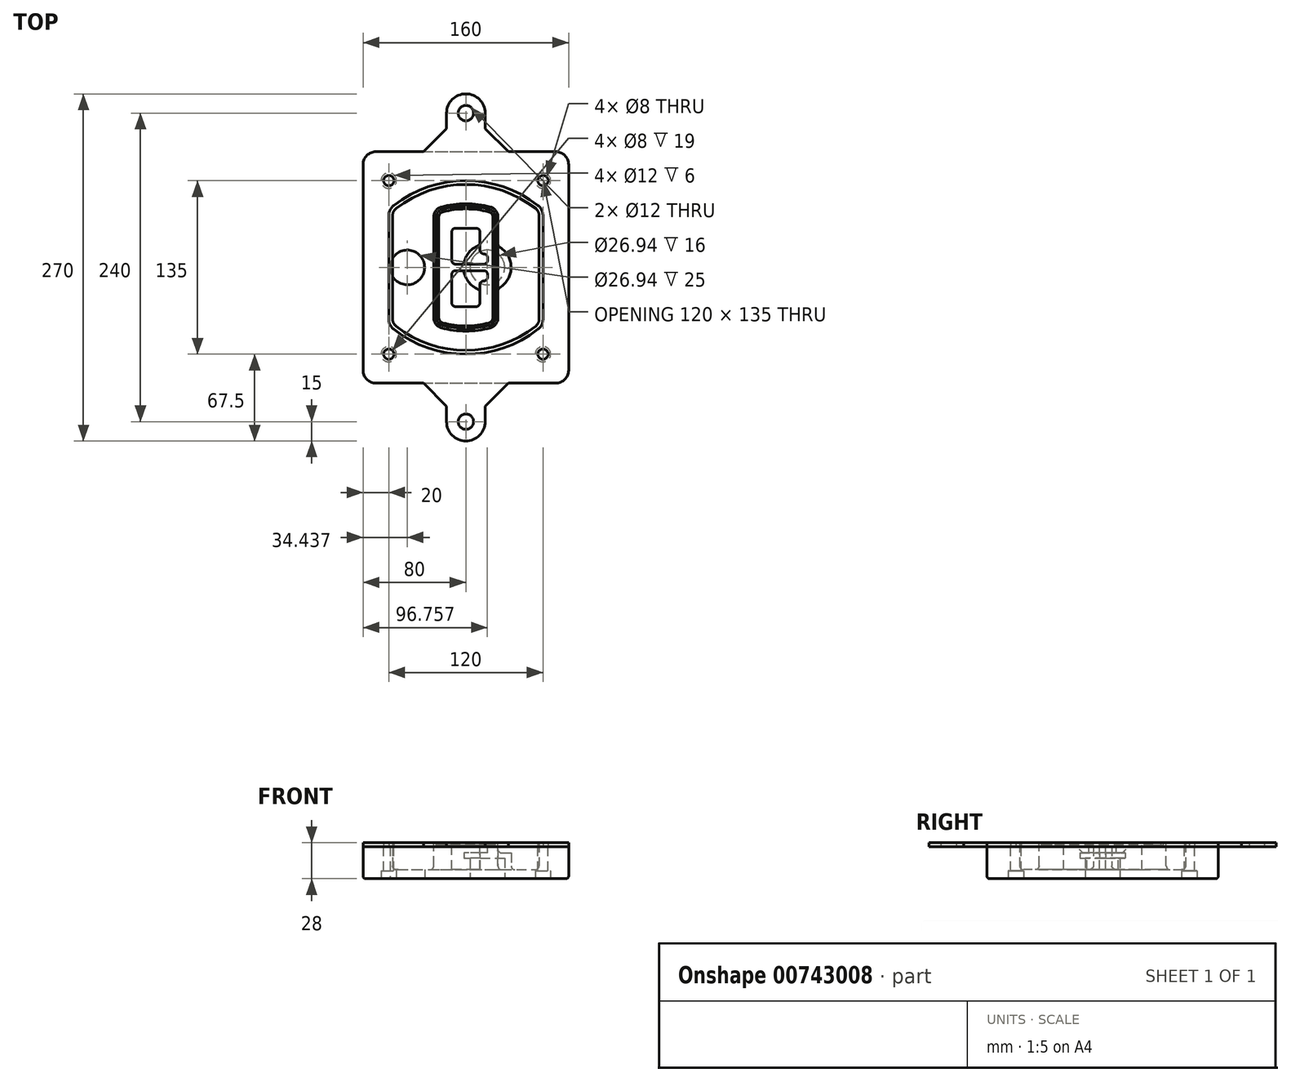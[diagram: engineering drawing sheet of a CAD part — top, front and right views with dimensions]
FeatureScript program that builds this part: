
annotation { "Feature Type Name" : "Feature", "Feature Type Description" : "" }
export const myFeature = defineFeature(function(context is Context, id is Id, definition is map)
    precondition{}
    {
        {
            var Q0;
            Q0=qCreatedBy(makeId("Top.planeOp"),FACE);
            var sketch = newSketch(context, id + "F0", { "sketchPlane" : qUnion([Q0])});
            skPoint(sketch, "E0.rect.middle", {"position": v(0, 0) * mm});
            skLineSegment(sketch, "E1.bottom", {"start": v(-70, -90) * mm, "end": v(70, -90) * mm});
            skLineSegment(sketch, "E1.top", {"start": v(-70, 90) * mm, "end": v(70, 90) * mm});
            skLineSegment(sketch, "E1.left", {"start": v(-80, -80) * mm, "end": v(-80, 80) * mm});
            skLineSegment(sketch, "E1.right", {"start": v(80, -80) * mm, "end": v(80, 80) * mm});
            skLineSegment(sketch, "E2", {"start": v(-80, 90) * mm, "end": v(80, -90) * mm, "construction": true});
            skLineSegment(sketch, "E3", {"start": v(80, 90) * mm, "end": v(-80, -90) * mm, "construction": true});
            skCircle(sketch, "E4", {"center": v(-60, 67.5) * mm, "radius": 4 * mm});
            skCircle(sketch, "E5", {"center": v(60, 67.5) * mm, "radius": 4 * mm});
            skCircle(sketch, "E6", {"center": v(60, -67.5) * mm, "radius": 4 * mm});
            skCircle(sketch, "E7", {"center": v(-60, -67.5) * mm, "radius": 4 * mm});
            skLineSegment(sketch, "E8", {"start": v(-60, 67.5) * mm, "end": v(60, 67.5) * mm, "construction": true});
            skLineSegment(sketch, "E9", {"start": v(60, 67.5) * mm, "end": v(60, -67.5) * mm, "construction": true});
            skLineSegment(sketch, "E10", {"start": v(60, -67.5) * mm, "end": v(-60, -67.5) * mm, "construction": true});
            skLineSegment(sketch, "E11", {"start": v(-60, -67.5) * mm, "end": v(-60, 67.5) * mm, "construction": true});
            skLineSegment(sketch, "E12", {"start": v(-60, 40.3) * mm, "end": v(-60, -40.3) * mm});
            skLineSegment(sketch, "E13", {"start": v(60, 40.3) * mm, "end": v(60, -40.3) * mm});
            skArc(sketch, "E14", {"start": v(56.15, 48.18) * mm, "mid": v(0, 67.5) * mm, "end": v(-56.15, 48.18) * mm});
            skArc(sketch, "E15", {"start": v(-56.15, -48.18) * mm, "mid": v(0, -67.5) * mm, "end": v(56.15, -48.18) * mm});
            skLineSegment(sketch, "E16", {"start": v(-60, 0) * mm, "end": v(60, 0) * mm, "construction": true});
            skPoint(sketch, "E17.visualSharp", {"position": v(-60, -45) * mm});
            skArc(sketch, "E17.filletArc", {"start": v(-60, -40.3) * mm, "mid": v(-58.99, -44.68) * mm, "end": v(-56.15, -48.18) * mm});
            skPoint(sketch, "E18.visualSharp", {"position": v(-60, 45) * mm});
            skArc(sketch, "E18.filletArc", {"start": v(-56.15, 48.18) * mm, "mid": v(-58.99, 44.68) * mm, "end": v(-60, 40.3) * mm});
            skPoint(sketch, "E19.visualSharp", {"position": v(60, 45) * mm});
            skArc(sketch, "E19.filletArc", {"start": v(60, 40.3) * mm, "mid": v(58.99, 44.68) * mm, "end": v(56.15, 48.18) * mm});
            skPoint(sketch, "E20.visualSharp", {"position": v(60, -45) * mm});
            skArc(sketch, "E20.filletArc", {"start": v(56.15, -48.18) * mm, "mid": v(58.99, -44.68) * mm, "end": v(60, -40.3) * mm});
            skPoint(sketch, "E21.visualSharp", {"position": v(-80, 90) * mm});
            skArc(sketch, "E21.filletArc", {"start": v(-70, 90) * mm, "mid": v(-77.07, 87.07) * mm, "end": v(-80, 80) * mm});
            skPoint(sketch, "E22.visualSharp", {"position": v(80, 90) * mm});
            skArc(sketch, "E22.filletArc", {"start": v(80, 80) * mm, "mid": v(77.07, 87.07) * mm, "end": v(70, 90) * mm});
            skPoint(sketch, "E23.visualSharp", {"position": v(80, -90) * mm});
            skArc(sketch, "E23.filletArc", {"start": v(70, -90) * mm, "mid": v(77.07, -87.07) * mm, "end": v(80, -80) * mm});
            skPoint(sketch, "E24.visualSharp", {"position": v(-80, -90) * mm});
            skArc(sketch, "E24.filletArc", {"start": v(-80, -80) * mm, "mid": v(-77.07, -87.07) * mm, "end": v(-70, -90) * mm});
            skArc(sketch, "E25.0", {"start": v(57, 40.3) * mm, "mid": v(56.3, 43.36) * mm, "end": v(54.3, 45.81) * mm});
            skLineSegment(sketch, "E25.1", {"start": v(57, 40.3) * mm, "end": v(57, -40.3) * mm});
            skArc(sketch, "E25.2", {"start": v(54.3, -45.81) * mm, "mid": v(56.3, -43.36) * mm, "end": v(57, -40.3) * mm});
            skArc(sketch, "E25.3", {"start": v(-54.3, -45.81) * mm, "mid": v(0, -64.5) * mm, "end": v(54.3, -45.81) * mm});
            skArc(sketch, "E25.4", {"start": v(-57, -40.3) * mm, "mid": v(-56.3, -43.36) * mm, "end": v(-54.3, -45.81) * mm});
            skArc(sketch, "E25.5", {"start": v(54.3, 45.81) * mm, "mid": v(0, 64.5) * mm, "end": v(-54.3, 45.81) * mm});
            skLineSegment(sketch, "E25.6", {"start": v(-57, 40.3) * mm, "end": v(-57, -40.3) * mm});
            skArc(sketch, "E25.7", {"start": v(-54.3, 45.81) * mm, "mid": v(-56.3, 43.36) * mm, "end": v(-57, 40.3) * mm});
            skArc(sketch, "E26.0", {"start": v(-58.62, 51.33) * mm, "mid": v(-62.58, 46.43) * mm, "end": v(-64, 40.3) * mm});
            skArc(sketch, "E26.1", {"start": v(58.62, 51.33) * mm, "mid": v(0, 71.5) * mm, "end": v(-58.62, 51.33) * mm});
            skArc(sketch, "E26.2", {"start": v(64, 40.3) * mm, "mid": v(62.58, 46.43) * mm, "end": v(58.62, 51.33) * mm});
            skLineSegment(sketch, "E26.3", {"start": v(64, 40.3) * mm, "end": v(64, -40.3) * mm});
            skArc(sketch, "E26.4", {"start": v(58.62, -51.33) * mm, "mid": v(62.58, -46.43) * mm, "end": v(64, -40.3) * mm});
            skLineSegment(sketch, "E26.5", {"start": v(-64, 40.3) * mm, "end": v(-64, -40.3) * mm});
            skArc(sketch, "E26.6", {"start": v(-58.62, -51.33) * mm, "mid": v(0, -71.5) * mm, "end": v(58.62, -51.33) * mm});
            skArc(sketch, "E26.7", {"start": v(-64, -40.3) * mm, "mid": v(-62.58, -46.43) * mm, "end": v(-58.62, -51.33) * mm});
            skSolve(sketch);
        }
        {
            var Q0;
            Q0=makeQuery(id+"F0.imprint","IMPRINT",FACE,{"disambiguationData":[TD([[makeQuery(id+"F0.imprint","IMPRINT",EDGE,{"derivedFrom":sQuery(id+"F0.wireOp",EDGE,"E1.bottom")}),1.0]])]});
            var Q1;
            Q1=makeQuery(id+"F0.imprint","IMPRINT",FACE,{"disambiguationData":[TD([[makeQuery(id+"F0.imprint","IMPRINT",EDGE,{"derivedFrom":sQuery(id+"F0.wireOp",EDGE,"E12")}),1.0]])]});
            var Q2;
            Q2=makeQuery(id+"F0.imprint","IMPRINT",FACE,{"disambiguationData":[TD([[makeQuery(id+"F0.imprint","IMPRINT",EDGE,{"derivedFrom":sQuery(id+"F0.wireOp",EDGE,"E25.0")}),1.0]])]});
            var Q3;
            Q3=makeQuery(id+"F0.imprint","IMPRINT",FACE,{"disambiguationData":[TD([[makeQuery(id+"F0.imprint","IMPRINT",EDGE,{"derivedFrom":sQuery(id+"F0.wireOp",EDGE,"E12")}),-1.0]])]});
            extrude(context, id + "F1", {"entities" : qUnion([Q0, Q1, Q2, Q3]), "oppositeDirection" : true, "depth" : 25 * mm, "offsetDistance" : 25 * mm});
        }
        {
            var Q0;
            Q0=makeQuery(id+"F0.imprint","IMPRINT",FACE,{"disambiguationData":[TD([[makeQuery(id+"F0.imprint","IMPRINT",EDGE,{"derivedFrom":sQuery(id+"F0.wireOp",EDGE,"E12")}),1.0]])]});
            extrude(context, id + "F2", {"entities" : qUnion([Q0]), "operationType" : NewBodyOperationType.ADD, "depth" : 3 * mm, "offsetDistance" : 25 * mm});
        }
        {
            var Q0;
            Q0=makeQuery(id+"F0.imprint","IMPRINT",FACE,{"disambiguationData":[TD([[makeQuery(id+"F0.imprint","IMPRINT",EDGE,{"derivedFrom":sQuery(id+"F0.wireOp",EDGE,"E25.0")}),1.0]])]});
            extrude(context, id + "F3", {"entities" : qUnion([Q0]), "operationType" : NewBodyOperationType.REMOVE, "oppositeDirection" : true, "depth" : 18 * mm});
        }
        {
            var Q0;
            Q0=makeQuery(id+"F2.opExtrude","CAP_FACE",FACE,{"disambiguationData":[OSD([sQuery(id+"F0.wireOp",EDGE,"E12"),sQuery(id+"F0.wireOp",EDGE,"E13"),sQuery(id+"F0.wireOp",EDGE,"E14"),sQuery(id+"F0.wireOp",EDGE,"E15"),sQuery(id+"F0.wireOp",EDGE,"E17.filletArc"),sQuery(id+"F0.wireOp",EDGE,"E18.filletArc"),sQuery(id+"F0.wireOp",EDGE,"E19.filletArc"),sQuery(id+"F0.wireOp",EDGE,"E20.filletArc"),sQuery(id+"F0.wireOp",EDGE,"E25.0"),sQuery(id+"F0.wireOp",EDGE,"E25.1"),sQuery(id+"F0.wireOp",EDGE,"E25.2"),sQuery(id+"F0.wireOp",EDGE,"E25.3"),sQuery(id+"F0.wireOp",EDGE,"E25.4"),sQuery(id+"F0.wireOp",EDGE,"E25.5"),sQuery(id+"F0.wireOp",EDGE,"E25.6"),sQuery(id+"F0.wireOp",EDGE,"E25.7")])],"isStart":false});
            var sketch = newSketch(context, id + "F4", { "sketchPlane" : qUnion([Q0])});
            skArc(sketch, "E27.0", {"start": v(-19.08, -46.97) * mm, "mid": v(0, -49.5) * mm, "end": v(19.08, -46.97) * mm});
            skArc(sketch, "E28.0", {"start": v(19.08, 46.97) * mm, "mid": v(0, 49.5) * mm, "end": v(-19.08, 46.97) * mm});
            skLineSegment(sketch, "E29", {"start": v(-25, 39.25) * mm, "end": v(-25, -39.25) * mm});
            skLineSegment(sketch, "E30", {"start": v(25, 39.25) * mm, "end": v(25, -39.25) * mm});
            skLineSegment(sketch, "E31", {"start": v(-25, 45.1) * mm, "end": v(25, 45.1) * mm, "construction": true});
            skLineSegment(sketch, "E32", {"start": v(-25, -45.1) * mm, "end": v(25, -45.1) * mm, "construction": true});
            skPoint(sketch, "E33.visualSharp", {"position": v(-25, 45.1) * mm});
            skArc(sketch, "E33.filletArc", {"start": v(-19.08, 46.97) * mm, "mid": v(-23.35, 44.11) * mm, "end": v(-25, 39.25) * mm});
            skPoint(sketch, "E34.visualSharp", {"position": v(25, 45.1) * mm});
            skArc(sketch, "E34.filletArc", {"start": v(25, 39.25) * mm, "mid": v(23.35, 44.11) * mm, "end": v(19.08, 46.97) * mm});
            skPoint(sketch, "E35.visualSharp", {"position": v(25, -45.1) * mm});
            skArc(sketch, "E35.filletArc", {"start": v(19.08, -46.97) * mm, "mid": v(23.35, -44.11) * mm, "end": v(25, -39.25) * mm});
            skPoint(sketch, "E36.visualSharp", {"position": v(-25, -45.1) * mm});
            skArc(sketch, "E36.filletArc", {"start": v(-25, -39.25) * mm, "mid": v(-23.35, -44.11) * mm, "end": v(-19.08, -46.97) * mm});
            skArc(sketch, "E37.0", {"start": v(54.3, 45.81) * mm, "mid": v(0, 64.5) * mm, "end": v(-54.3, 45.81) * mm});
            skArc(sketch, "E37.1", {"start": v(-54.3, 45.81) * mm, "mid": v(-56.3, 43.36) * mm, "end": v(-57, 40.3) * mm});
            skLineSegment(sketch, "E37.2", {"start": v(-57, 40.3) * mm, "end": v(-57, -40.3) * mm});
            skArc(sketch, "E37.3", {"start": v(-57, -40.3) * mm, "mid": v(-56.3, -43.36) * mm, "end": v(-54.3, -45.81) * mm});
            skArc(sketch, "E37.4", {"start": v(-54.3, -45.81) * mm, "mid": v(0, -64.5) * mm, "end": v(54.3, -45.81) * mm});
            skArc(sketch, "E37.5", {"start": v(54.3, -45.81) * mm, "mid": v(56.3, -43.36) * mm, "end": v(57, -40.3) * mm});
            skLineSegment(sketch, "E37.6", {"start": v(57, 40.3) * mm, "end": v(57, -40.3) * mm});
            skArc(sketch, "E37.7", {"start": v(57, 40.3) * mm, "mid": v(56.3, 43.36) * mm, "end": v(54.3, 45.81) * mm});
            skLineSegment(sketch, "E38.0", {"start": v(23, 39.25) * mm, "end": v(23, -39.25) * mm});
            skArc(sketch, "E38.1", {"start": v(18.56, -45.04) * mm, "mid": v(21.76, -42.9) * mm, "end": v(23, -39.25) * mm});
            skArc(sketch, "E38.2", {"start": v(-18.56, -45.04) * mm, "mid": v(0, -47.5) * mm, "end": v(18.56, -45.04) * mm});
            skArc(sketch, "E38.3", {"start": v(-23, -39.25) * mm, "mid": v(-21.76, -42.9) * mm, "end": v(-18.56, -45.04) * mm});
            skLineSegment(sketch, "E38.4", {"start": v(-23, 39.25) * mm, "end": v(-23, -39.25) * mm});
            skArc(sketch, "E38.5", {"start": v(23, 39.25) * mm, "mid": v(21.76, 42.9) * mm, "end": v(18.56, 45.04) * mm});
            skArc(sketch, "E38.6", {"start": v(-18.56, 45.04) * mm, "mid": v(-21.76, 42.9) * mm, "end": v(-23, 39.25) * mm});
            skArc(sketch, "E38.7", {"start": v(18.56, 45.04) * mm, "mid": v(0, 47.5) * mm, "end": v(-18.56, 45.04) * mm});
            skArc(sketch, "E39.0", {"start": v(21, 39.25) * mm, "mid": v(20.18, 41.68) * mm, "end": v(18.04, 43.1) * mm});
            skLineSegment(sketch, "E39.1", {"start": v(21, 39.25) * mm, "end": v(21, -39.25) * mm});
            skArc(sketch, "E39.2", {"start": v(18.04, -43.1) * mm, "mid": v(20.18, -41.68) * mm, "end": v(21, -39.25) * mm});
            skArc(sketch, "E39.3", {"start": v(-18.04, -43.1) * mm, "mid": v(0, -45.5) * mm, "end": v(18.04, -43.1) * mm});
            skArc(sketch, "E39.4", {"start": v(-21, -39.25) * mm, "mid": v(-20.18, -41.68) * mm, "end": v(-18.04, -43.1) * mm});
            skArc(sketch, "E39.5", {"start": v(18.04, 43.1) * mm, "mid": v(0, 45.5) * mm, "end": v(-18.04, 43.1) * mm});
            skLineSegment(sketch, "E39.6", {"start": v(-21, 39.25) * mm, "end": v(-21, -39.25) * mm});
            skArc(sketch, "E39.7", {"start": v(-18.04, 43.1) * mm, "mid": v(-20.18, 41.68) * mm, "end": v(-21, 39.25) * mm});
            skLineSegment(sketch, "E40", {"start": v(-25, 0) * mm, "end": v(25, 0) * mm, "construction": true});
            skLineSegment(sketch, "E41", {"start": v(-11, 5.5) * mm, "end": v(-11, 27.5) * mm});
            skLineSegment(sketch, "E42", {"start": v(-8, 30.5) * mm, "end": v(8, 30.5) * mm});
            skLineSegment(sketch, "E43", {"start": v(11, 27.5) * mm, "end": v(11, 13.5) * mm});
            skLineSegment(sketch, "E44", {"start": v(14, 10.5) * mm, "end": v(14, 10.5) * mm});
            skLineSegment(sketch, "E45", {"start": v(17, 7.5) * mm, "end": v(17, 5.5) * mm});
            skLineSegment(sketch, "E46", {"start": v(14, 2.5) * mm, "end": v(-8, 2.5) * mm});
            skPoint(sketch, "E47.visualSharp", {"position": v(-11, 30.5) * mm});
            skArc(sketch, "E47.filletArc", {"start": v(-8, 30.5) * mm, "mid": v(-10.12, 29.62) * mm, "end": v(-11, 27.5) * mm});
            skPoint(sketch, "E48.visualSharp", {"position": v(11, 30.5) * mm});
            skArc(sketch, "E48.filletArc", {"start": v(11, 27.5) * mm, "mid": v(10.12, 29.62) * mm, "end": v(8, 30.5) * mm});
            skPoint(sketch, "E49.visualSharp", {"position": v(11, 10.5) * mm});
            skArc(sketch, "E49.filletArc", {"start": v(11, 13.5) * mm, "mid": v(11.88, 11.38) * mm, "end": v(14, 10.5) * mm});
            skPoint(sketch, "E50.visualSharp", {"position": v(17, 10.5) * mm});
            skArc(sketch, "E50.filletArc", {"start": v(17, 7.5) * mm, "mid": v(16.12, 9.62) * mm, "end": v(14, 10.5) * mm});
            skPoint(sketch, "E51.visualSharp", {"position": v(17, 2.5) * mm});
            skArc(sketch, "E51.filletArc", {"start": v(14, 2.5) * mm, "mid": v(16.12, 3.38) * mm, "end": v(17, 5.5) * mm});
            skPoint(sketch, "E52.visualSharp", {"position": v(-11, 2.5) * mm});
            skArc(sketch, "E52.filletArc", {"start": v(-11, 5.5) * mm, "mid": v(-10.12, 3.38) * mm, "end": v(-8, 2.5) * mm});
            skLineSegment(sketch, "E53.0.MirrorCS", {"start": v(14, -2.5) * mm, "end": v(-8, -2.5) * mm});
            skArc(sketch, "E54.0.MirrorCS", {"start": v(-11, -5.5) * mm, "mid": v(-10.12, -3.38) * mm, "end": v(-8, -2.5) * mm});
            skLineSegment(sketch, "E55.0.MirrorCS", {"start": v(-11, -5.5) * mm, "end": v(-11, -27.5) * mm});
            skArc(sketch, "E56.0.MirrorCS", {"start": v(-8, -30.5) * mm, "mid": v(-10.12, -29.62) * mm, "end": v(-11, -27.5) * mm});
            skLineSegment(sketch, "E57.0.MirrorCS", {"start": v(-8, -30.5) * mm, "end": v(8, -30.5) * mm});
            skArc(sketch, "E58.0.MirrorCS", {"start": v(11, -27.5) * mm, "mid": v(10.12, -29.62) * mm, "end": v(8, -30.5) * mm});
            skLineSegment(sketch, "E59.0.MirrorCS", {"start": v(11, -27.5) * mm, "end": v(11, -13.5) * mm});
            skArc(sketch, "E60.0.MirrorCS", {"start": v(11, -13.5) * mm, "mid": v(11.88, -11.38) * mm, "end": v(14, -10.5) * mm});
            skArc(sketch, "E61.0.MirrorCS", {"start": v(17, -7.5) * mm, "mid": v(16.12, -9.62) * mm, "end": v(14, -10.5) * mm});
            skLineSegment(sketch, "E62.0.MirrorCS", {"start": v(17, -7.5) * mm, "end": v(17, -5.5) * mm});
            skArc(sketch, "E63.0.MirrorCS", {"start": v(14, -2.5) * mm, "mid": v(16.12, -3.38) * mm, "end": v(17, -5.5) * mm});
            skSolve(sketch);
        }
        {
            var Q0;
            Q0=makeQuery(id+"F4.imprint","IMPRINT",FACE,{"disambiguationData":[TD([[makeQuery(id+"F4.imprint","IMPRINT",EDGE,{"derivedFrom":sQuery(id+"F4.wireOp",EDGE,"E27.0")}),1.0]])]});
            var Q1;
            Q1=makeQuery(id+"F4.imprint","IMPRINT",FACE,{"disambiguationData":[TD([[makeQuery(id+"F4.imprint","IMPRINT",EDGE,{"derivedFrom":sQuery(id+"F4.wireOp",EDGE,"E38.0")}),-1.0]])]});
            var Q2;
            Q2=makeQuery(id+"F4.imprint","IMPRINT",FACE,{"disambiguationData":[TD([[makeQuery(id+"F4.imprint","IMPRINT",EDGE,{"derivedFrom":sQuery(id+"F4.wireOp",EDGE,"E39.0")}),1.0]])]});
            extrude(context, id + "F5", {"entities" : qUnion([Q0, Q1, Q2]), "operationType" : NewBodyOperationType.ADD, "endBound" : BoundingType.UP_TO_NEXT, "oppositeDirection" : true, "depth" : 25 * mm});
        }
        {
            var Q0;
            Q0=makeQuery(id+"F4.imprint","IMPRINT",FACE,{"disambiguationData":[TD([[makeQuery(id+"F4.imprint","IMPRINT",EDGE,{"derivedFrom":sQuery(id+"F4.wireOp",EDGE,"E38.0")}),-1.0]])]});
            extrude(context, id + "F6", {"entities" : qUnion([Q0]), "operationType" : NewBodyOperationType.REMOVE, "oppositeDirection" : true, "depth" : 2 * mm});
        }
        {
            var Q0;
            Q0=makeQuery(id+"F1.opExtrude","CAP_FACE",FACE,{"disambiguationData":[OSD([sQuery(id+"F0.wireOp",EDGE,"E1.bottom"),sQuery(id+"F0.wireOp",EDGE,"E1.top"),sQuery(id+"F0.wireOp",EDGE,"E1.left"),sQuery(id+"F0.wireOp",EDGE,"E1.right"),sQuery(id+"F0.wireOp",EDGE,"E4"),sQuery(id+"F0.wireOp",EDGE,"E5"),sQuery(id+"F0.wireOp",EDGE,"E6"),sQuery(id+"F0.wireOp",EDGE,"E7"),sQuery(id+"F0.wireOp",EDGE,"E21.filletArc"),sQuery(id+"F0.wireOp",EDGE,"E22.filletArc"),sQuery(id+"F0.wireOp",EDGE,"E23.filletArc"),sQuery(id+"F0.wireOp",EDGE,"E24.filletArc")])],"isStart":false});
            var sketch = newSketch(context, id + "F7", { "sketchPlane" : qUnion([Q0])});
            skCircle(sketch, "E64", {"center": v(16.76, 0) * mm, "radius": 13.47 * mm});
            skCircle(sketch, "E65", {"center": v(-45.56, 0) * mm, "radius": 13.47 * mm});
            skLineSegment(sketch, "E66", {"start": v(80, 0) * mm, "end": v(-80, 0) * mm});
            skCircle(sketch, "E67", {"center": v(16.76, 0) * mm, "radius": 18.47 * mm});
            skCircle(sketch, "E68", {"center": v(60, -67.5) * mm, "radius": 6 * mm});
            skCircle(sketch, "E69", {"center": v(-60, -67.5) * mm, "radius": 6 * mm});
            skCircle(sketch, "E70", {"center": v(-60, 67.5) * mm, "radius": 6 * mm});
            skCircle(sketch, "E71", {"center": v(60, 67.5) * mm, "radius": 6 * mm});
            skSolve(sketch);
        }
        {
            var Q0;
            {var subQ1=sQuery(id+"F7.wireOp",EDGE,"E66");var subQ4=sQuery(id+"F7.wireOp",EDGE,"E64");var subQ6=makeQuery(id+"F7.imprint","INTERSECT",VERTEX,{"disambiguationData":[OD(0.0)],"derivedFrom":[subQ4,subQ1]});Q0=makeQuery(id+"F7.imprint","IMPRINT",FACE,{"disambiguationData":[TD([[makeQuery(id+"F7.imprint","IMPRINT",EDGE,{"disambiguationData":[TD([[subQ6,-1.0]])],"derivedFrom":subQ4}),-1.0]])]});}
            var Q1;
            {var subQ0=sQuery(id+"F7.wireOp",EDGE,"E66");var subQ1=sQuery(id+"F7.wireOp",EDGE,"E64");var subQ3=makeQuery(id+"F7.imprint","INTERSECT",VERTEX,{"disambiguationData":[OD(0.0)],"derivedFrom":[subQ1,subQ0]});Q1=makeQuery(id+"F7.imprint","IMPRINT",FACE,{"disambiguationData":[TD([[makeQuery(id+"F7.imprint","IMPRINT",EDGE,{"disambiguationData":[TD([[subQ3,-1.0]])],"derivedFrom":subQ1}),1.0]])]});}
            var Q2;
            {var subQ0=sQuery(id+"F7.wireOp",EDGE,"E66");var subQ1=sQuery(id+"F7.wireOp",EDGE,"E64");var subQ3=makeQuery(id+"F7.imprint","INTERSECT",VERTEX,{"disambiguationData":[OD(0.0)],"derivedFrom":[subQ1,subQ0]});Q2=makeQuery(id+"F7.imprint","IMPRINT",FACE,{"disambiguationData":[TD([[makeQuery(id+"F7.imprint","IMPRINT",EDGE,{"disambiguationData":[TD([[subQ3,1.0]])],"derivedFrom":subQ1}),1.0]])]});}
            var Q3;
            {var subQ1=sQuery(id+"F7.wireOp",EDGE,"E66");var subQ4=sQuery(id+"F7.wireOp",EDGE,"E64");var subQ6=makeQuery(id+"F7.imprint","INTERSECT",VERTEX,{"disambiguationData":[OD(0.0)],"derivedFrom":[subQ4,subQ1]});Q3=makeQuery(id+"F7.imprint","IMPRINT",FACE,{"disambiguationData":[TD([[makeQuery(id+"F7.imprint","IMPRINT",EDGE,{"disambiguationData":[TD([[subQ6,1.0]])],"derivedFrom":subQ4}),-1.0]])]});}
            extrude(context, id + "F8", {"entities" : qUnion([Q0, Q1, Q2, Q3]), "operationType" : NewBodyOperationType.ADD, "oppositeDirection" : true, "depth" : 20 * mm});
        }
        {
            var Q0;
            {var subQ0=sQuery(id+"F7.wireOp",EDGE,"E66");var subQ1=sQuery(id+"F7.wireOp",EDGE,"E64");var subQ3=makeQuery(id+"F7.imprint","INTERSECT",VERTEX,{"disambiguationData":[OD(0.0)],"derivedFrom":[subQ1,subQ0]});Q0=makeQuery(id+"F7.imprint","IMPRINT",FACE,{"disambiguationData":[TD([[makeQuery(id+"F7.imprint","IMPRINT",EDGE,{"disambiguationData":[TD([[subQ3,-1.0]])],"derivedFrom":subQ1}),1.0]])]});}
            var Q1;
            {var subQ0=sQuery(id+"F7.wireOp",EDGE,"E66");var subQ1=sQuery(id+"F7.wireOp",EDGE,"E64");var subQ3=makeQuery(id+"F7.imprint","INTERSECT",VERTEX,{"disambiguationData":[OD(0.0)],"derivedFrom":[subQ1,subQ0]});Q1=makeQuery(id+"F7.imprint","IMPRINT",FACE,{"disambiguationData":[TD([[makeQuery(id+"F7.imprint","IMPRINT",EDGE,{"disambiguationData":[TD([[subQ3,1.0]])],"derivedFrom":subQ1}),1.0]])]});}
            extrude(context, id + "F9", {"entities" : qUnion([Q0, Q1]), "operationType" : NewBodyOperationType.REMOVE, "oppositeDirection" : true, "depth" : 16 * mm});
        }
        {
            var Q0;
            {var subQ0=sQuery(id+"F7.wireOp",EDGE,"E66");var subQ1=sQuery(id+"F7.wireOp",EDGE,"E65");var subQ3=makeQuery(id+"F7.imprint","INTERSECT",VERTEX,{"disambiguationData":[OD(0.0)],"derivedFrom":[subQ1,subQ0]});Q0=makeQuery(id+"F7.imprint","IMPRINT",FACE,{"disambiguationData":[TD([[makeQuery(id+"F7.imprint","IMPRINT",EDGE,{"disambiguationData":[TD([[subQ3,-1.0]])],"derivedFrom":subQ1}),1.0]])]});}
            var Q1;
            {var subQ0=sQuery(id+"F7.wireOp",EDGE,"E66");var subQ1=sQuery(id+"F7.wireOp",EDGE,"E65");var subQ3=makeQuery(id+"F7.imprint","INTERSECT",VERTEX,{"disambiguationData":[OD(0.0)],"derivedFrom":[subQ1,subQ0]});Q1=makeQuery(id+"F7.imprint","IMPRINT",FACE,{"disambiguationData":[TD([[makeQuery(id+"F7.imprint","IMPRINT",EDGE,{"disambiguationData":[TD([[subQ3,1.0]])],"derivedFrom":subQ1}),1.0]])]});}
            extrude(context, id + "F10", {"entities" : qUnion([Q0, Q1]), "operationType" : NewBodyOperationType.REMOVE, "oppositeDirection" : true, "depth" : 25 * mm});
        }
        {
            var Q0;
            Q0=makeQuery(id+"F7.imprint","IMPRINT",FACE,{"disambiguationData":[TD([[makeQuery(id+"F7.imprint","IMPRINT",EDGE,{"derivedFrom":sQuery(id+"F7.wireOp",EDGE,"E68")}),1.0]])]});
            var Q1;
            Q1=makeQuery(id+"F7.imprint","IMPRINT",FACE,{"disambiguationData":[TD([[makeQuery(id+"F7.imprint","IMPRINT",EDGE,{"derivedFrom":makeQuery(id+"F1.opExtrude","CAP_EDGE",EDGE,{"disambiguationData":[OSD([sQuery(id+"F0.wireOp",EDGE,"E5")])],"isStart":false})}),-1.0]])]});
            var Q2;
            Q2=makeQuery(id+"F7.imprint","IMPRINT",FACE,{"disambiguationData":[TD([[makeQuery(id+"F7.imprint","IMPRINT",EDGE,{"derivedFrom":sQuery(id+"F7.wireOp",EDGE,"E69")}),1.0]])]});
            var Q3;
            Q3=makeQuery(id+"F7.imprint","IMPRINT",FACE,{"disambiguationData":[TD([[makeQuery(id+"F7.imprint","IMPRINT",EDGE,{"derivedFrom":makeQuery(id+"F1.opExtrude","CAP_EDGE",EDGE,{"disambiguationData":[OSD([sQuery(id+"F0.wireOp",EDGE,"E4")])],"isStart":false})}),-1.0]])]});
            var Q4;
            Q4=makeQuery(id+"F7.imprint","IMPRINT",FACE,{"disambiguationData":[TD([[makeQuery(id+"F7.imprint","IMPRINT",EDGE,{"derivedFrom":sQuery(id+"F7.wireOp",EDGE,"E70")}),1.0]])]});
            var Q5;
            Q5=makeQuery(id+"F7.imprint","IMPRINT",FACE,{"disambiguationData":[TD([[makeQuery(id+"F7.imprint","IMPRINT",EDGE,{"derivedFrom":makeQuery(id+"F1.opExtrude","CAP_EDGE",EDGE,{"disambiguationData":[OSD([sQuery(id+"F0.wireOp",EDGE,"E7")])],"isStart":false})}),-1.0]])]});
            var Q6;
            Q6=makeQuery(id+"F7.imprint","IMPRINT",FACE,{"disambiguationData":[TD([[makeQuery(id+"F7.imprint","IMPRINT",EDGE,{"derivedFrom":sQuery(id+"F7.wireOp",EDGE,"E71")}),1.0]])]});
            var Q7;
            Q7=makeQuery(id+"F7.imprint","IMPRINT",FACE,{"disambiguationData":[TD([[makeQuery(id+"F7.imprint","IMPRINT",EDGE,{"derivedFrom":makeQuery(id+"F1.opExtrude","CAP_EDGE",EDGE,{"disambiguationData":[OSD([sQuery(id+"F0.wireOp",EDGE,"E6")])],"isStart":false})}),-1.0]])]});
            extrude(context, id + "F11", {"entities" : qUnion([Q0, Q1, Q2, Q3, Q4, Q5, Q6, Q7]), "operationType" : NewBodyOperationType.REMOVE, "oppositeDirection" : true, "depth" : 6 * mm});
        }
        {
            var Q0;
            Q0=makeQuery(id+"F9.boolean.opBoolean","COPY",FACE,{"derivedFrom":makeQuery(id+"F9.opExtrude","CAP_FACE",FACE,{"disambiguationData":[OSD([sQuery(id+"F7.wireOp",EDGE,"E64")])],"isStart":false})});
            var sketch = newSketch(context, id + "F12", { "sketchPlane" : qUnion([Q0])});
            skArc(sketch, "E72.0", {"start": v(11, 17.55) * mm, "mid": v(2.57, 11.82) * mm, "end": v(-1.54, 2.5) * mm});
            skArc(sketch, "E72.1", {"start": v(-1.54, -2.5) * mm, "mid": v(2.57, -11.82) * mm, "end": v(11, -17.55) * mm});
            skLineSegment(sketch, "E73", {"start": v(-1.54, -2.5) * mm, "end": v(14, -2.5) * mm});
            skLineSegment(sketch, "E74.0", {"start": v(14, 2.5) * mm, "end": v(-1.54, 2.5) * mm});
            skArc(sketch, "E74.1", {"start": v(14, 2.5) * mm, "mid": v(16.12, 3.38) * mm, "end": v(17, 5.5) * mm});
            skLineSegment(sketch, "E74.2", {"start": v(17, 7.5) * mm, "end": v(17, 5.5) * mm});
            skArc(sketch, "E74.3", {"start": v(17, 7.5) * mm, "mid": v(16.12, 9.62) * mm, "end": v(14, 10.5) * mm});
            skArc(sketch, "E74.4", {"start": v(11, 13.5) * mm, "mid": v(11.88, 11.38) * mm, "end": v(14, 10.5) * mm});
            skLineSegment(sketch, "E74.5", {"start": v(11, 17.55) * mm, "end": v(11, 13.5) * mm});
            skLineSegment(sketch, "E74.7", {"start": v(14, -2.5) * mm, "end": v(-1.54, -2.5) * mm});
            skArc(sketch, "E74.8", {"start": v(14, -2.5) * mm, "mid": v(16.12, -3.38) * mm, "end": v(17, -5.5) * mm});
            skLineSegment(sketch, "E74.9", {"start": v(17, -7.5) * mm, "end": v(17, -5.5) * mm});
            skArc(sketch, "E74.10", {"start": v(17, -7.5) * mm, "mid": v(16.12, -9.62) * mm, "end": v(14, -10.5) * mm});
            skArc(sketch, "E74.11", {"start": v(11, -13.5) * mm, "mid": v(11.88, -11.38) * mm, "end": v(14, -10.5) * mm});
            skLineSegment(sketch, "E74.12", {"start": v(11, -17.55) * mm, "end": v(11, -13.5) * mm});
            skPoint(sketch, "E75.orphan", {"position": v(11, -27.5) * mm});
            skPoint(sketch, "E76.orphan", {"position": v(-8, -2.5) * mm});
            skPoint(sketch, "E77.orphan", {"position": v(-8, 2.5) * mm});
            skPoint(sketch, "E78.orphan", {"position": v(11, 27.5) * mm});
            skSolve(sketch);
        }
        {
            var Q0;
            {var subQ7=sQuery(id+"F12.wireOp",EDGE,"E72.0");var subQ14=sQuery(id+"F12.wireOp",EDGE,"E72.1");var subQ16=sQuery(id+"F12.wireOp",EDGE,"E74.1");var subQ18=sQuery(id+"F12.wireOp",EDGE,"E74.8");Q0=qUnion([makeQuery(id+"F12.imprint","IMPRINT",FACE,{"disambiguationData":[TD([[makeQuery(id+"F12.imprint","IMPRINT",EDGE,{"derivedFrom":subQ7}),1.0]])]}),makeQuery(id+"F12.imprint","IMPRINT",FACE,{"disambiguationData":[TD([[makeQuery(id+"F12.imprint","IMPRINT",EDGE,{"derivedFrom":subQ14}),1.0]])]}),makeQuery(id+"F12.imprint","IMPRINT",FACE,{"disambiguationData":[TD([[makeQuery(id+"F12.imprint","IMPRINT",EDGE,{"derivedFrom":subQ16}),1.0]])]}),makeQuery(id+"F12.imprint","IMPRINT",FACE,{"disambiguationData":[TD([[makeQuery(id+"F12.imprint","IMPRINT",EDGE,{"derivedFrom":subQ18}),-1.0]])]})]);}
            var Q1;
            Q1=makeQuery(id+"F5.boolean.opBoolean","SPLIT",FACE,{"disambiguationData":[TD([makeQuery(id+"F5.opExtrude","SWEPT_FACE",FACE,{"disambiguationData":[OSD([sQuery(id+"F4.wireOp",EDGE,"E41")])]})])],"derivedFrom":makeQuery(id+"F3.boolean.opBoolean","COPY",FACE,{"derivedFrom":makeQuery(id+"F3.opExtrude","CAP_FACE",FACE,{"disambiguationData":[OSD([sQuery(id+"F0.wireOp",EDGE,"E25.0"),sQuery(id+"F0.wireOp",EDGE,"E25.1"),sQuery(id+"F0.wireOp",EDGE,"E25.2"),sQuery(id+"F0.wireOp",EDGE,"E25.3"),sQuery(id+"F0.wireOp",EDGE,"E25.4"),sQuery(id+"F0.wireOp",EDGE,"E25.5"),sQuery(id+"F0.wireOp",EDGE,"E25.6"),sQuery(id+"F0.wireOp",EDGE,"E25.7")])],"isStart":false})})});
            extrude(context, id + "F13", {"entities" : qUnion([Q0]), "operationType" : NewBodyOperationType.REMOVE, "endBound" : BoundingType.UP_TO_SURFACE, "endBoundEntityFace" : qUnion([Q1]), "depth" : 25 * mm});
        }
        {
            var Q0;
            Q0=makeQuery(id+"F3.boolean.opBoolean","COPY",EDGE,{"derivedFrom":makeQuery(id+"F3.opExtrude","CAP_EDGE",EDGE,{"disambiguationData":[OSD([sQuery(id+"F0.wireOp",EDGE,"E25.6")])],"isStart":false})});
            var Q1;
            Q1=makeQuery(id+"F8.boolean.opBoolean","INTERSECT",EDGE,{"derivedFrom":[makeQuery(id+"F5.opExtrude","SWEPT_FACE",FACE,{"disambiguationData":[OSD([sQuery(id+"F4.wireOp",EDGE,"E30")])]}),makeQuery(id+"F8.opExtrude","CAP_FACE",FACE,{"disambiguationData":[OSD([sQuery(id+"F7.wireOp",EDGE,"E67")])],"isStart":false})]});
            var Q2;
            Q2=makeQuery(id+"F8.boolean.opBoolean","INTERSECT",EDGE,{"disambiguationData":[OD(1.0)],"derivedFrom":[makeQuery(id+"F5.opExtrude","SWEPT_FACE",FACE,{"disambiguationData":[OSD([sQuery(id+"F4.wireOp",EDGE,"E30")])]}),makeQuery(id+"F8.opExtrude","SWEPT_FACE",FACE,{"disambiguationData":[OSD([sQuery(id+"F7.wireOp",EDGE,"E67")])]})]});
            var Q3;
            {var subQ0=sQuery(id+"F4.wireOp",EDGE,"E30");Q3=makeQuery(id+"F8.boolean.opBoolean","SPLIT",EDGE,{"disambiguationData":[TD([makeQuery(id+"F5.opExtrude","SWEPT_FACE",FACE,{"disambiguationData":[OSD([sQuery(id+"F4.wireOp",EDGE,"E35.filletArc")])]})])],"derivedFrom":makeQuery(id+"F5.opExtrude","CAP_EDGE",EDGE,{"disambiguationData":[OSD([subQ0])],"isStart":false})});}
            var Q4;
            {var subQ0=sQuery(id+"F0.wireOp",EDGE,"E25.7");var subQ1=sQuery(id+"F0.wireOp",EDGE,"E25.1");var subQ2=sQuery(id+"F0.wireOp",EDGE,"E25.6");var subQ3=sQuery(id+"F0.wireOp",EDGE,"E25.5");var subQ4=sQuery(id+"F0.wireOp",EDGE,"E25.4");var subQ5=sQuery(id+"F0.wireOp",EDGE,"E25.0");var subQ6=sQuery(id+"F0.wireOp",EDGE,"E25.2");var subQ7=sQuery(id+"F0.wireOp",EDGE,"E25.3");Q4=makeQuery(id+"F8.boolean.opBoolean","INTERSECT",EDGE,{"derivedFrom":[makeQuery(id+"F5.boolean.opBoolean","SPLIT",FACE,{"disambiguationData":[TD([makeQuery(id+"F2.opExtrude","SWEPT_FACE",FACE,{"disambiguationData":[OSD([subQ5])]})])],"derivedFrom":makeQuery(id+"F3.boolean.opBoolean","COPY",FACE,{"derivedFrom":makeQuery(id+"F3.opExtrude","CAP_FACE",FACE,{"disambiguationData":[OSD([subQ5,subQ1,subQ6,subQ7,subQ4,subQ3,subQ2,subQ0])],"isStart":false})})}),makeQuery(id+"F8.opExtrude","SWEPT_FACE",FACE,{"disambiguationData":[OSD([sQuery(id+"F7.wireOp",EDGE,"E67")])]})]});}
            var Q5;
            Q5=makeQuery(id+"F8.boolean.opBoolean","INTERSECT",EDGE,{"disambiguationData":[OD(0.0)],"derivedFrom":[makeQuery(id+"F5.opExtrude","SWEPT_FACE",FACE,{"disambiguationData":[OSD([sQuery(id+"F4.wireOp",EDGE,"E30")])]}),makeQuery(id+"F8.opExtrude","SWEPT_FACE",FACE,{"disambiguationData":[OSD([sQuery(id+"F7.wireOp",EDGE,"E67")])]})]});
            fillet(context, id + "F14", {"entities" : qUnion([Q0, Q1, Q2, Q3, Q4, Q5]), "radius" : 3 * mm, "tangentPropagation" : true, "allowEdgeOverflow" : false});
        }
        {
            var Q0;
            Q0=makeQuery(id+"F1.opExtrude","CAP_EDGE",EDGE,{"disambiguationData":[OSD([sQuery(id+"F0.wireOp",EDGE,"E1.bottom")])],"isStart":false});
            fillet(context, id + "F15", {"entities" : qUnion([Q0]), "radius" : 2 * mm, "tangentPropagation" : true, "allowEdgeOverflow" : false});
        }
        {
            var Q0;
            {var subQ0=sQuery(id+"F0.wireOp",EDGE,"E21.filletArc");var subQ1=sQuery(id+"F0.wireOp",EDGE,"E7");var subQ2=sQuery(id+"F0.wireOp",EDGE,"E6");var subQ3=sQuery(id+"F0.wireOp",EDGE,"E5");var subQ4=sQuery(id+"F0.wireOp",EDGE,"E4");var subQ5=sQuery(id+"F0.wireOp",EDGE,"E22.filletArc");var subQ6=sQuery(id+"F0.wireOp",EDGE,"E1.bottom");var subQ7=sQuery(id+"F0.wireOp",EDGE,"E1.right");var subQ8=sQuery(id+"F0.wireOp",EDGE,"E1.top");var subQ9=sQuery(id+"F0.wireOp",EDGE,"E1.left");var subQ10=sQuery(id+"F0.wireOp",EDGE,"E23.filletArc");var subQ11=sQuery(id+"F0.wireOp",EDGE,"E24.filletArc");Q0=makeQuery(id+"F2.boolean.opBoolean","SPLIT",FACE,{"disambiguationData":[TD([makeQuery(id+"F1.opExtrude","SWEPT_FACE",FACE,{"disambiguationData":[OSD([subQ6])]})])],"derivedFrom":makeQuery(id+"F1.opExtrude","CAP_FACE",FACE,{"disambiguationData":[OSD([subQ6,subQ8,subQ9,subQ7,subQ4,subQ3,subQ2,subQ1,subQ0,subQ5,subQ10,subQ11])],"isStart":true})});}
            var sketch = newSketch(context, id + "F16", { "sketchPlane" : qUnion([Q0])});
            skLineSegment(sketch, "E79", {"start": v(0, 90) * mm, "end": v(0, 91.07) * mm, "construction": true});
            skLineSegment(sketch, "E80", {"start": v(0, 90) * mm, "end": v(0, 120) * mm, "construction": true});
            skCircle(sketch, "E81", {"center": v(0, 120) * mm, "radius": 6 * mm});
            skArc(sketch, "E82", {"start": v(15, 120) * mm, "mid": v(0, 135) * mm, "end": v(-15, 120) * mm});
            skPoint(sketch, "E83.endSnap0", {"position": v(0, 105) * mm});
            skLineSegment(sketch, "E84", {"start": v(-15, 120) * mm, "end": v(-15, 108) * mm});
            skLineSegment(sketch, "E85", {"start": v(15, 120) * mm, "end": v(15, 108) * mm});
            skLineSegment(sketch, "E86", {"start": v(-15, 108) * mm, "end": v(-33, 90) * mm});
            skLineSegment(sketch, "E87", {"start": v(15, 108) * mm, "end": v(33, 90) * mm});
            skLineSegment(sketch, "E88", {"start": v(-80, 0) * mm, "end": v(80, 0) * mm, "construction": true});
            skLineSegment(sketch, "E89.MirrorCS", {"start": v(15, -108) * mm, "end": v(33, -90) * mm});
            skLineSegment(sketch, "E90.MirrorCS", {"start": v(15, -120) * mm, "end": v(15, -108) * mm});
            skArc(sketch, "E91.MirrorCS", {"start": v(15, -120) * mm, "mid": v(0, -135) * mm, "end": v(-15, -120) * mm});
            skLineSegment(sketch, "E92.MirrorCS", {"start": v(-15, -120) * mm, "end": v(-15, -108) * mm});
            skLineSegment(sketch, "E93.MirrorCS", {"start": v(-15, -108) * mm, "end": v(-33, -90) * mm});
            skCircle(sketch, "E94.MirrorC", {"center": v(0, -120) * mm, "radius": 6 * mm});
            skLineSegment(sketch, "E95.MirrorCS", {"start": v(0, -90) * mm, "end": v(0, -120) * mm, "construction": true});
            skSolve(sketch);
        }
        {
            var Q0;
            Q0=makeQuery(id+"F16.imprint","IMPRINT",FACE,{"disambiguationData":[TD([[makeQuery(id+"F16.imprint","IMPRINT",EDGE,{"derivedFrom":sQuery(id+"F16.wireOp",EDGE,"E81")}),-1.0]])]});
            var Q1;
            Q1=makeQuery(id+"F16.imprint","IMPRINT",FACE,{"disambiguationData":[TD([[makeQuery(id+"F16.imprint","IMPRINT",EDGE,{"derivedFrom":makeQuery(id+"F1.opExtrude","CAP_EDGE",EDGE,{"disambiguationData":[OSD([sQuery(id+"F0.wireOp",EDGE,"E1.left")])],"isStart":true})}),-1.0]])]});
            var Q2;
            {var subQ0=sQuery(id+"F16.wireOp",EDGE,"E89.MirrorCS");Q2=makeQuery(id+"F16.imprint","IMPRINT",FACE,{"disambiguationData":[TD([[makeQuery(id+"F16.imprint","IMPRINT",EDGE,{"derivedFrom":subQ0}),1.0]])]});}
            var Q3;
            Q3=makeQuery(id+"F2.opExtrude","CAP_FACE",FACE,{"disambiguationData":[OSD([sQuery(id+"F0.wireOp",EDGE,"E12"),sQuery(id+"F0.wireOp",EDGE,"E13"),sQuery(id+"F0.wireOp",EDGE,"E14"),sQuery(id+"F0.wireOp",EDGE,"E15"),sQuery(id+"F0.wireOp",EDGE,"E17.filletArc"),sQuery(id+"F0.wireOp",EDGE,"E18.filletArc"),sQuery(id+"F0.wireOp",EDGE,"E19.filletArc"),sQuery(id+"F0.wireOp",EDGE,"E20.filletArc"),sQuery(id+"F0.wireOp",EDGE,"E25.0"),sQuery(id+"F0.wireOp",EDGE,"E25.1"),sQuery(id+"F0.wireOp",EDGE,"E25.2"),sQuery(id+"F0.wireOp",EDGE,"E25.3"),sQuery(id+"F0.wireOp",EDGE,"E25.4"),sQuery(id+"F0.wireOp",EDGE,"E25.5"),sQuery(id+"F0.wireOp",EDGE,"E25.6"),sQuery(id+"F0.wireOp",EDGE,"E25.7")])],"isStart":false});
            extrude(context, id + "F17", {"entities" : qUnion([Q0, Q1, Q2]), "endBound" : BoundingType.UP_TO_SURFACE, "depth" : 25 * mm, "endBoundEntityFace" : qUnion([Q3]), "offsetDistance" : 25 * mm});
        }
    });
